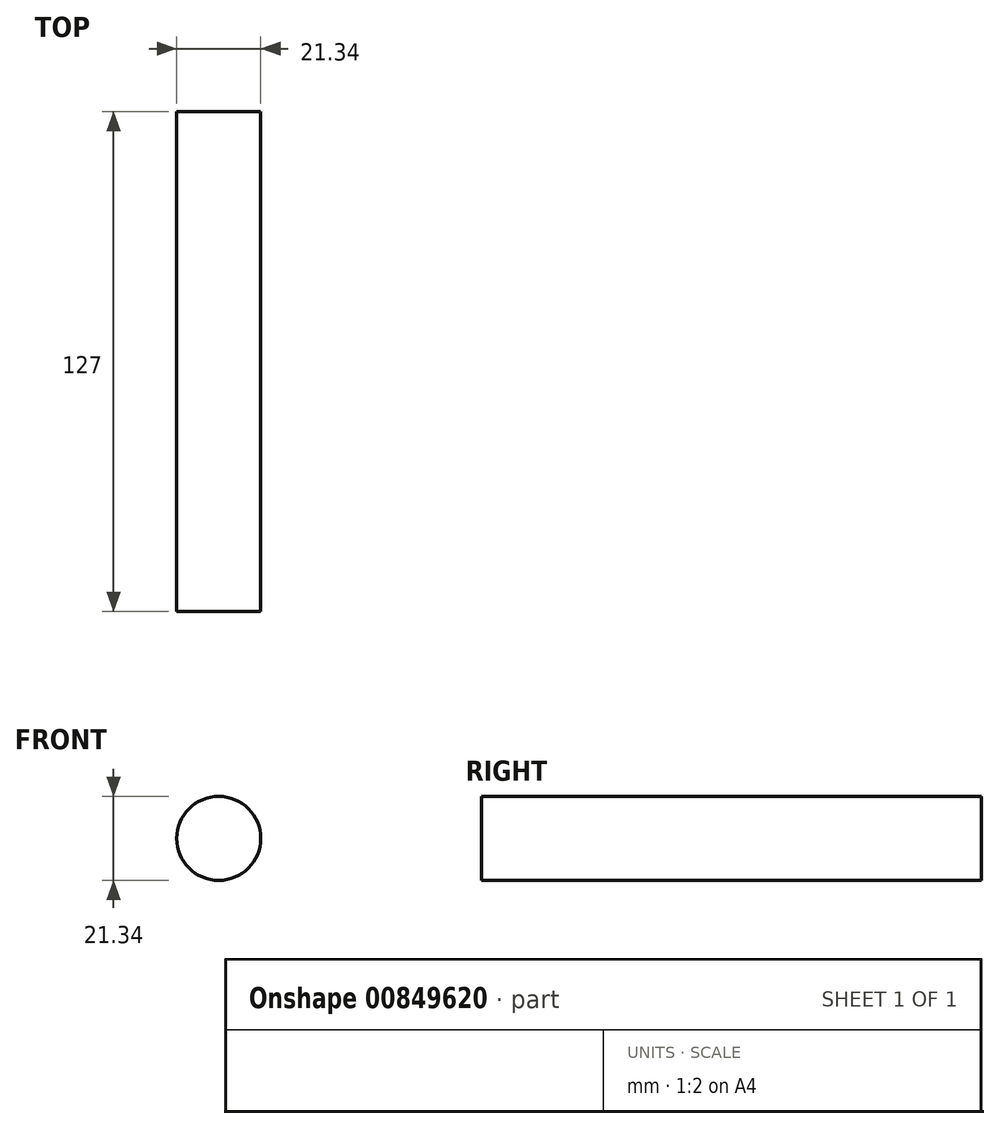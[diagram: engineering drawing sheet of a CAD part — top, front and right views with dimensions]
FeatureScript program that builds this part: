
annotation { "Feature Type Name" : "Feature", "Feature Type Description" : "" }
export const myFeature = defineFeature(function(context is Context, id is Id, definition is map)
    precondition{}
    {
        {
            var Q0;
            Q0=qCreatedBy(makeId("Front.planeOp"),FACE);
            var sketch = newSketch(context, id + "F0", { "sketchPlane" : qUnion([Q0])});
            skCircle(sketch, "E0", {"center": v(0, 0) * mm, "radius": 10.67 * mm});
            skSolve(sketch);
        }
        {
            var Q0;
            Q0=makeQuery(id+"F0.imprint","IMPRINT",FACE,{"disambiguationData":[TD([[makeQuery(id+"F0.imprint","IMPRINT",EDGE,{"derivedFrom":sQuery(id+"F0.wireOp",EDGE,"E0")}),1.0]])]});
            extrude(context, id + "F1", {"entities" : qUnion([Q0]), "depth" : 127 * mm, "offsetDistance" : 25.4 * mm});
        }
    });
